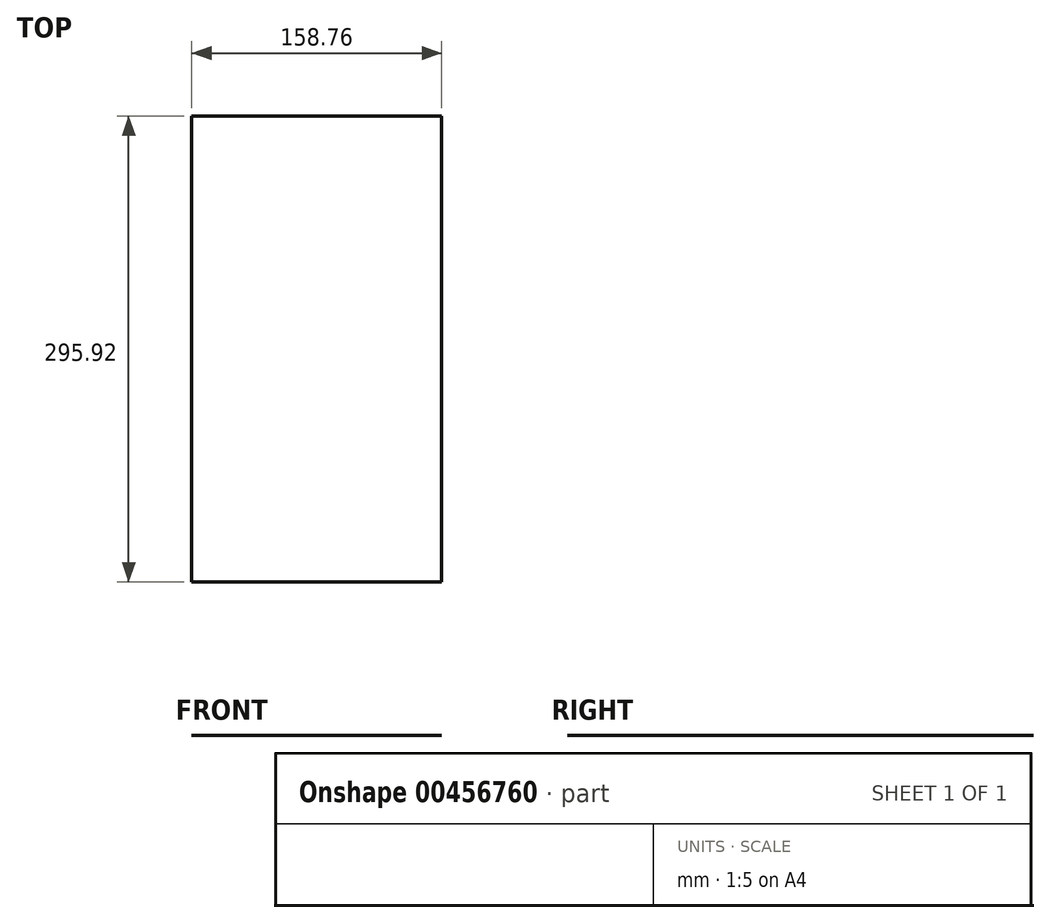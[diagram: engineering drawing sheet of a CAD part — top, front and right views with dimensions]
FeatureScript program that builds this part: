
annotation { "Feature Type Name" : "Feature", "Feature Type Description" : "" }
export const myFeature = defineFeature(function(context is Context, id is Id, definition is map)
    precondition{}
    {
        {
            var Q0;
            Q0=qCreatedBy(makeId("Top.planeOp"),FACE);
            var sketch = newSketch(context, id + "F0", { "sketchPlane" : qUnion([Q0])});
            skLineSegment(sketch, "E0.bottom", {"start": v(-79.37, 147.96) * mm, "end": v(79.38, 147.96) * mm});
            skLineSegment(sketch, "E0.top", {"start": v(-79.38, -147.96) * mm, "end": v(79.37, -147.96) * mm});
            skLineSegment(sketch, "E0.left", {"start": v(-79.37, 147.96) * mm, "end": v(-79.38, -147.96) * mm});
            skLineSegment(sketch, "E0.right", {"start": v(79.38, 147.96) * mm, "end": v(79.37, -147.96) * mm});
            skPoint(sketch, "E0.middle", {"position": v(0, 0) * mm});
            skSolve(sketch);
        }
        {
            var Q0;
            Q0=makeQuery(id+"F0.imprint","IMPRINT",FACE,{"disambiguationData":[TD([[makeQuery(id+"F0.imprint","IMPRINT",EDGE,{"derivedFrom":sQuery(id+"F0.wireOp",EDGE,"E0.bottom")}),-1.0]])]});
            extrude(context, id + "F1", {"entities" : qUnion([Q0]), "depth" : 1 / 203.2 * mm});
        }
    });
